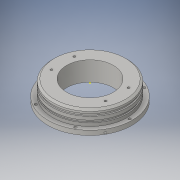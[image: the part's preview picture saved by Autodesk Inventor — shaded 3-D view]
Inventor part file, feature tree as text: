
AUTODESK INVENTOR PART (.ipt)
format: ipt  version: 2016 (Build 200138000, 138)  size: 336,896 bytes
history: native  units: in
note: dims shown in document units (in); Inventor stores cm internally (conversion verified against a paired STEP export)
features: sketch x23, extrude x20, plane x3, chamfer x2, fillet x1, revolve x1
ambient origin geometry x8: Origin, YZ Plane, XZ Plane, XY Plane, X Axis, Y Axis, Z Axis, Center Point
bodies: Solid1 (feature_tree)
feature tree (50):
  extrude  "Extrusion1"  Depth=0.3in TaperAngle=0.0deg
  extrude  "Extrusion2"  Depth=0.125in TaperAngle=0.0deg
  extrude  "Extrusion3"  Depth=3.875in
  sketch  "Sketch4"  dims[d9=0.125in d10=0.0in d11=4.0in]
  extrude  "Extrusion4"  Depth=4.0in
  extrude  "Extrusion5"  Depth=0.2in
  extrude  "Extrusion6"  Depth=0.24in TaperAngle=45.0deg
  chamfer  "Chamfer1"  Distance=2.3622in Angle=360.0deg
  extrude  "Extrusion7"  Depth=0.24in
  extrude  "Extrusion8"  Depth=5.0in TaperAngle=0.0deg
  extrude  "Extrusion9"  Depth=0.375in TaperAngle=0.0deg
  extrude  "Extrusion10"  Depth=0.375in TaperAngle=0.0deg
  extrude  "Extrusion11"  Depth=0.5in
  sketch  "Sketch13"  dims[d39=20.0in d40=0.0in d41=0.5in]
  extrude  "Extrusion12"  Depth=0.15in
  chamfer  "Chamfer2"  Distance=1.1811in Angle=360.0deg
  fillet  "Fillet1"  Radius=0.125in
  plane  "Work Plane1"
  revolve  "Revolution1"  [1 undecoded]
  plane  "Work Plane3"
  extrude  "Extrusion13"  [1 undecoded]
  extrude  "Extrusion14"  Depth=0.118in
  extrude  "Extrusion15"  Depth=0.118in
  extrude  "Extrusion16"  Depth=0.74in
  extrude  "Extrusion17"  Depth=0.74in
  extrude  "Extrusion18"  Depth=0.4in
  extrude  "Extrusion19"  Depth=0.4in
  extrude  "Extrusion20"  Depth=1.04in TaperAngle=0.0deg
  sketch  "Sketch1"  dims[d0=4.0in d1=0.3in d2=0.0in]
  sketch  "Sketch2"  dims[d3=3.875in d4=0.125in d5=0.0in]
  sketch  "Sketch3"  dims[d6=0.3in d7=0.0in d8=3.875in]
  sketch  "Sketch5"  dims[d12=0.2in d13=0.0in d14=4.5in]
  sketch  "Sketch6"  dims[d15=0.24in d16=0.0in d17=0.1in d18=0.125in d19=45.0deg]
  sketch  "Sketch7"  dims[d20=0.138in]
  sketch  "Sketch8"  dims[d21=2.125in d22=2.3622in d24=360.0deg]
  sketch  "Sketch9"  dims[d26=0.24in d27=0.0in d28=1.0in]
  sketch  "Sketch10"  dims[d29=0.1in d31=5.0in d32=0.0in]
  sketch  "Sketch11"  dims[d33=3.0in d34=0.375in d35=0.0in]
  sketch  "Sketch12"  dims[d36=1.0in d37=0.375in d38=0.0in]
  sketch  "Sketch14"  dims[d42=0.5in d43=0.15in d44=1.1811in d46=360.0deg]
  sketch  "Sketch15"  dims[d48=5.0in d49=0.2in d50=0.0in d51=0.0in]
  plane  "Work Plane2"
  sketch  "Sketch16"  dims[d52=0.125in d53=0.125in d54=45.0deg d55=0.125in]
  sketch  "Sketch17"  dims[d58=0.1in d59=1.527in]
  sketch  "Sketch18"  dims[d60=90.0deg d61=-4.125in]
  sketch  "Sketch19"  dims[d64=0.118in d65=0.118in]
  sketch  "Sketch20"  dims[d66=0.118in d67=0.118in]
  sketch  "Sketch21"  dims[d68=0.74in d69=0.74in]
  sketch  "Sketch22"  dims[d70=0.74in d71=0.74in]
  sketch  "Sketch23"  dims[d72=5.0in d73=0.0in d74=0.25in d75=0.5in d76=1.04in d77=0.0in d78=0.1181in d79=0.4in d80=0.0in d81=0.1181in d82=0.4in d83=0.0in d84=0.1181in d85=0.4in d86=0.0in d87=12.0in d88=12.0in d89=0.0in d90=0.0in d91=2.0in d92=0.0in d93=0.1181in d94=2.9in d95=0.1181in d96=0.1181in d97=0.1181in d98=1.229in d99=1.229in d100=0.4in d101=0.0in]
note: 2 required parameter values undecoded (feature->parameter linkage not recoverable at this tier; creation-order binding heuristic only, values carry confidence <= 0.55)